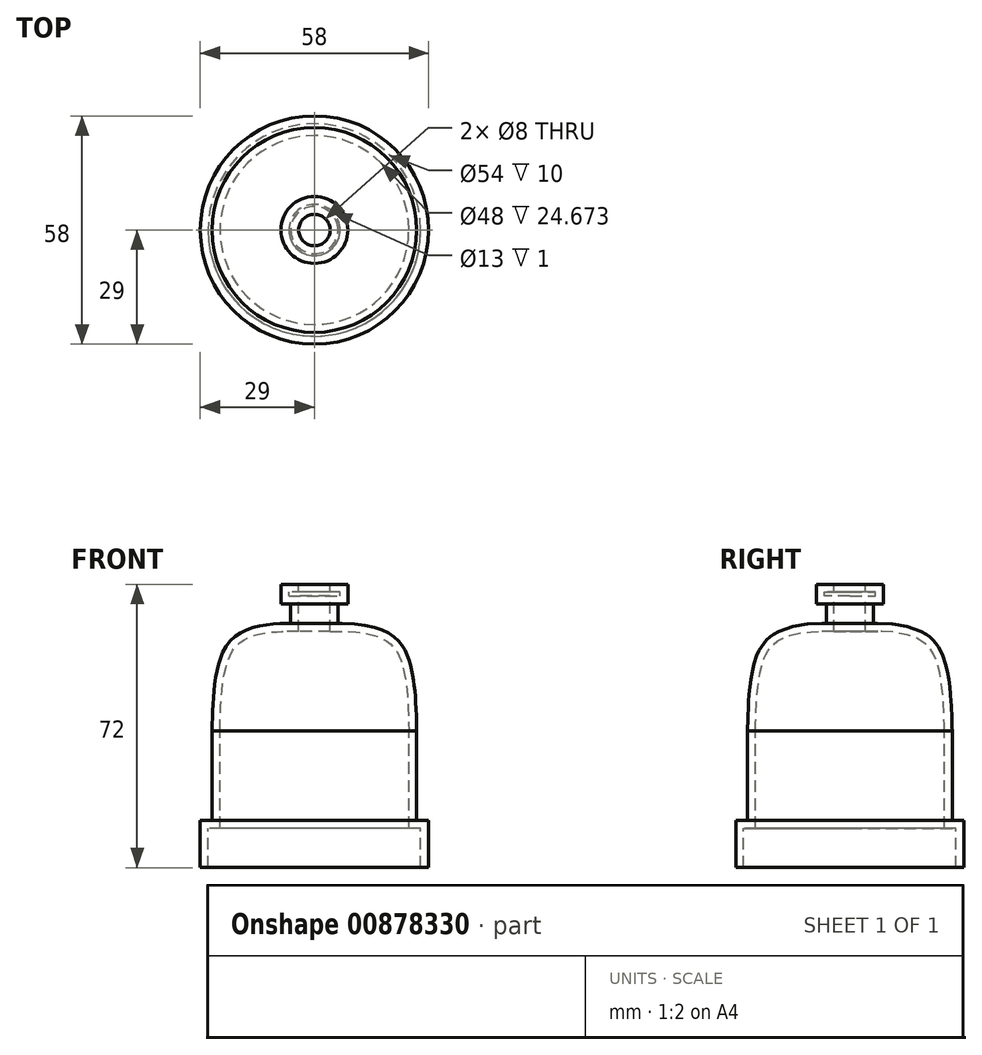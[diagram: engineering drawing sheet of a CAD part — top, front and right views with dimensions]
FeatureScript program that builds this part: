
annotation { "Feature Type Name" : "Feature", "Feature Type Description" : "" }
export const myFeature = defineFeature(function(context is Context, id is Id, definition is map)
    precondition{}
    {
        {
            var Q0;
            Q0=qCreatedBy(makeId("Right.planeOp"),FACE);
            var sketch = newSketch(context, id + "F0", { "sketchPlane" : qUnion([Q0])});
            skLineSegment(sketch, "E0", {"start": v(0, 52.3) * mm, "end": v(8.5, 52.3) * mm});
            skLineSegment(sketch, "E1", {"start": v(8.5, 52.3) * mm, "end": v(8.5, 47.3) * mm});
            skLineSegment(sketch, "E2", {"start": v(8.5, 47.3) * mm, "end": v(6, 47.3) * mm});
            skLineSegment(sketch, "E3", {"start": v(6, 47.3) * mm, "end": v(6, 42.3) * mm});
            skFitSpline(sketch, "E4", {"points": [v(6, 42.3) * mm, v(24.4, 31.7) * mm, v(26, 15) * mm], "startDerivative": vector(81.46, 1.63) * mm, "endDerivative": vector(1.32, -49.03) * mm});
            skLineSegment(sketch, "E5", {"start": v(26, 15) * mm, "end": v(26, -7.7) * mm});
            skLineSegment(sketch, "E6", {"start": v(26, -7.7) * mm, "end": v(29, -7.7) * mm});
            skLineSegment(sketch, "E7", {"start": v(29, -7.7) * mm, "end": v(29, -19.7) * mm});
            skLineSegment(sketch, "E8", {"start": v(29, -19.7) * mm, "end": v(0, -19.7) * mm});
            skLineSegment(sketch, "E9", {"start": v(0, -19.7) * mm, "end": v(0, 52.3) * mm});
            skLineSegment(sketch, "E10", {"start": v(0, 71.59) * mm, "end": v(0, -45.7) * mm, "construction": true});
            skSolve(sketch);
        }
        {
            var Q0;
            Q0 = qSketchRegion(id + "F0", true);
            var Q1;
            Q1=sQuery(id+"F0.wireOp",EDGE,"E10");
            revolve(context, id + "F1", {"surfaceOperationType" : NewSurfaceOperationType.NEW, "entities" : qUnion([Q0]), "axis" : qUnion([Q1]), "revolveType" : RevolveType.FULL});
        }
        {
            var Q0;
            Q0=makeQuery(id+"F1.opRevolve","SWEPT_FACE",FACE,{"disambiguationData":[OSD([sQuery(id+"F0.wireOp",EDGE,"E8")])]});
            shell(context, id + "F2", {"entities" : qUnion([Q0]), "thickness" : 2 * mm});
        }
        {
            var Q0;
            Q0=makeQuery(id+"F1.opRevolve","SWEPT_FACE",FACE,{"disambiguationData":[OSD([sQuery(id+"F0.wireOp",EDGE,"E0")])]});
            var sketch = newSketch(context, id + "F3", { "sketchPlane" : qUnion([Q0])});
            skCircle(sketch, "E11", {"center": v(0, 0) * mm, "radius": 4 * mm});
            skSolve(sketch);
        }
        {
            var Q0;
            Q0=makeQuery(id+"F3.imprint","IMPRINT",FACE,{"disambiguationData":[TD([[makeQuery(id+"F3.imprint","IMPRINT",EDGE,{"derivedFrom":sQuery(id+"F3.wireOp",EDGE,"E11")}),1.0]])]});
            extrude(context, id + "F4", {"entities" : qUnion([Q0]), "operationType" : NewBodyOperationType.REMOVE, "oppositeDirection" : true, "depth" : 15 * mm, "offsetDistance" : 25 * mm});
        }
    });
